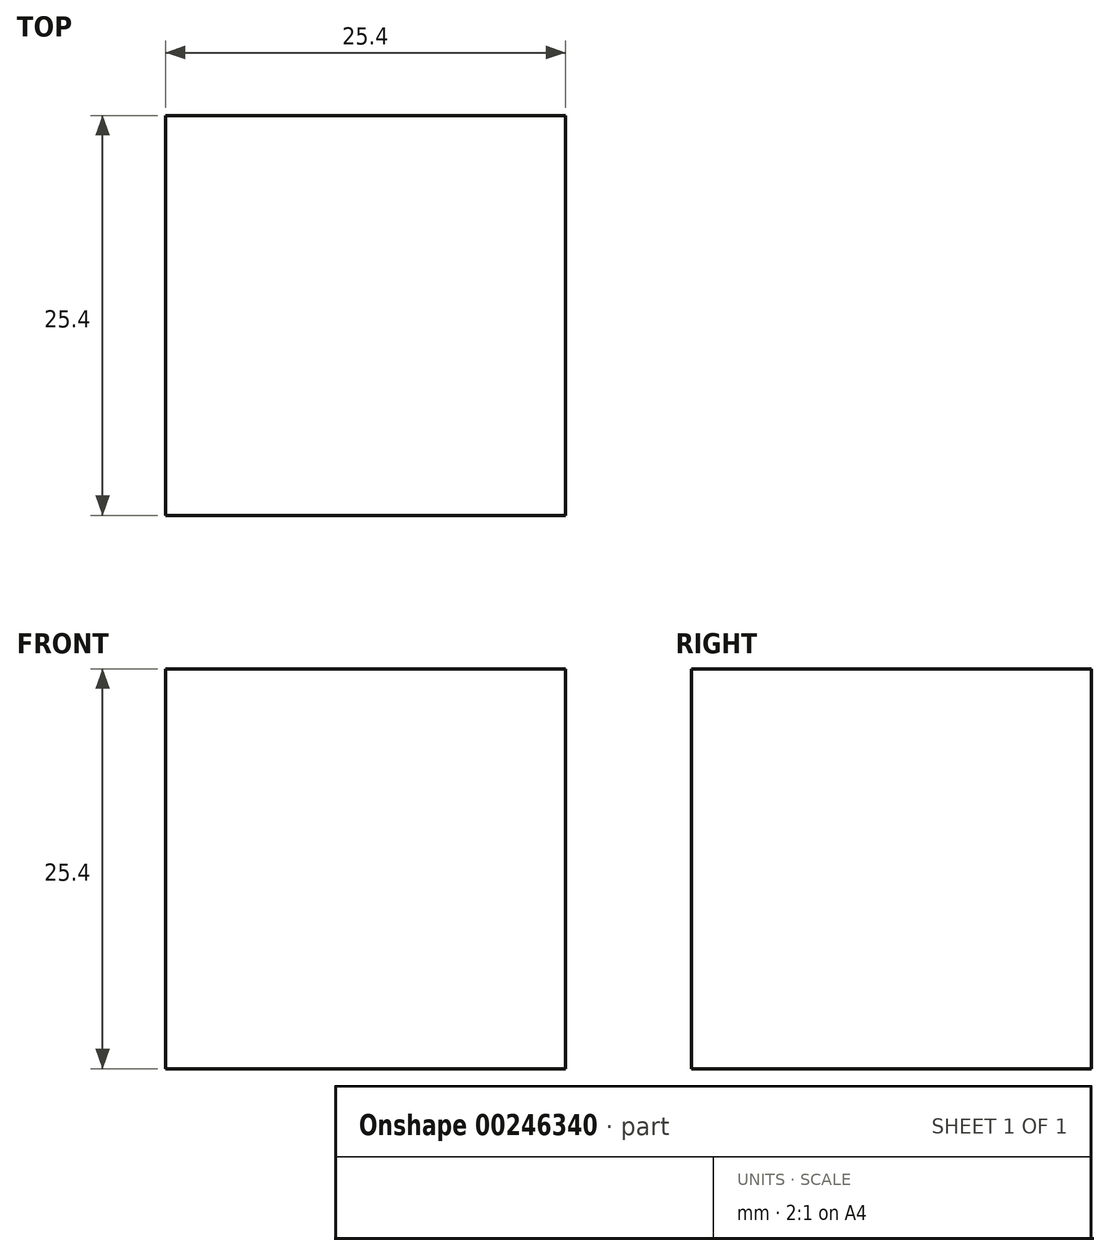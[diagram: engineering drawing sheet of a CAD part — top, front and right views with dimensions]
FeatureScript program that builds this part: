
annotation { "Feature Type Name" : "Feature", "Feature Type Description" : "" }
export const myFeature = defineFeature(function(context is Context, id is Id, definition is map)
    precondition{}
    {
        {
            var Q0;
            Q0=qCreatedBy(makeId("Top.planeOp"),FACE);
            var sketch = newSketch(context, id + "F0", { "sketchPlane" : qUnion([Q0])});
            skLineSegment(sketch, "E0.bottom", {"start": v(-19.63, 19.74) * mm, "end": v(5.77, 19.74) * mm});
            skLineSegment(sketch, "E0.top", {"start": v(-19.63, -5.66) * mm, "end": v(5.77, -5.66) * mm});
            skLineSegment(sketch, "E0.left", {"start": v(-19.63, 19.74) * mm, "end": v(-19.63, -5.66) * mm});
            skLineSegment(sketch, "E0.right", {"start": v(5.77, 19.74) * mm, "end": v(5.77, -5.66) * mm});
            skSolve(sketch);
        }
        {
            var Q0;
            Q0=makeQuery(id+"F0.imprint","IMPRINT",FACE,{"disambiguationData":[TD([[makeQuery(id+"F0.imprint","IMPRINT",EDGE,{"derivedFrom":sQuery(id+"F0.wireOp",EDGE,"E0.bottom")}),-1.0]])]});
            extrude(context, id + "F1", {"entities" : qUnion([Q0]), "depth" : 25.4 * mm});
        }
    });
